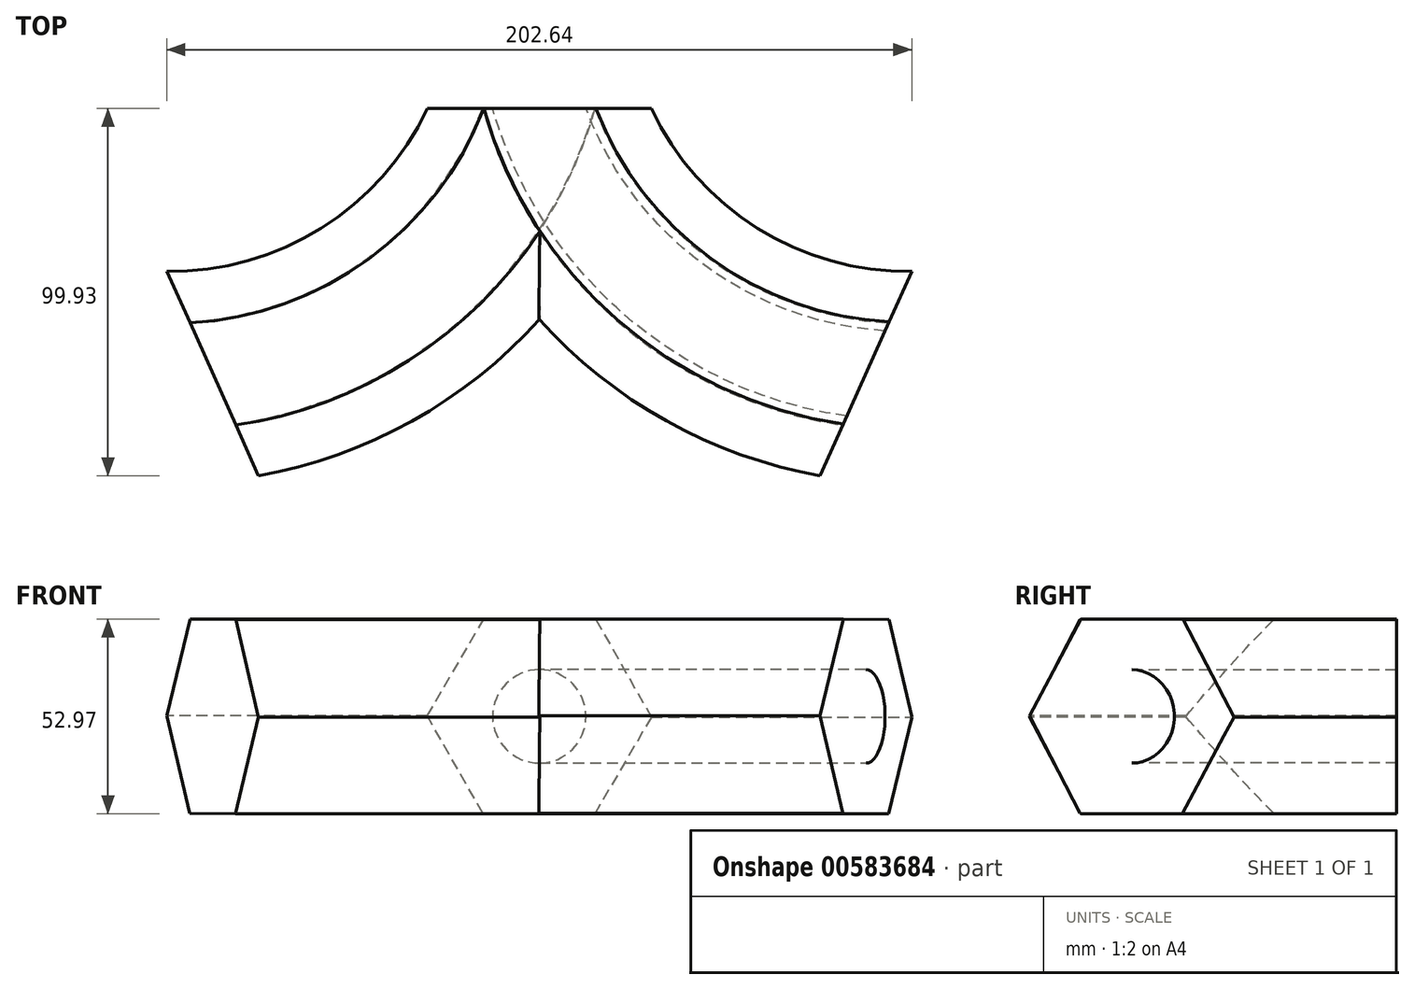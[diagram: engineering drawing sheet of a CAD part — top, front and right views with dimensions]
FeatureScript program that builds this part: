
annotation { "Feature Type Name" : "Feature", "Feature Type Description" : "" }
export const myFeature = defineFeature(function(context is Context, id is Id, definition is map)
    precondition{}
    {
        {
            var Q0;
            Q0=qCreatedBy(makeId("Front.planeOp"),FACE);
            var sketch = newSketch(context, id + "F0", { "sketchPlane" : qUnion([Q0])});
            skCircle(sketch, "E0.cCircle", {"center": v(0, 26.89) * mm, "radius": 26.4 * mm, "construction": true});
            skLineSegment(sketch, "E0.0", {"start": v(-15.4, 0.58) * mm, "end": v(-30.48, 27.07) * mm});
            skLineSegment(sketch, "E0.1", {"start": v(-30.48, 27.07) * mm, "end": v(-15.08, 53.37) * mm});
            skLineSegment(sketch, "E0.2", {"start": v(-15.08, 53.37) * mm, "end": v(15.4, 53.2) * mm});
            skLineSegment(sketch, "E0.3", {"start": v(15.4, 53.2) * mm, "end": v(30.48, 26.7) * mm});
            skLineSegment(sketch, "E0.4", {"start": v(30.48, 26.7) * mm, "end": v(15.08, 0.4) * mm});
            skLineSegment(sketch, "E0.5", {"start": v(15.08, 0.4) * mm, "end": v(-15.4, 0.58) * mm});
            skPoint(sketch, "E0.0.midPoint", {"position": v(-22.94, 13.82) * mm});
            skCircle(sketch, "E1", {"center": v(0, 26.89) * mm, "radius": 12.7 * mm});
            skSolve(sketch);
        }
        {
            var Q0;
            Q0=qCreatedBy(makeId("Top.planeOp"),FACE);
            var sketch = newSketch(context, id + "F1", { "sketchPlane" : qUnion([Q0])});
            skArc(sketch, "E2", {"start": v(-88.86, -72.11) * mm, "mid": v(-33.77, -49.2) * mm, "end": v(0, 0) * mm});
            skArc(sketch, "E3.MirrorCS", {"start": v(88.86, -72.11) * mm, "mid": v(33.77, -49.2) * mm, "end": v(0, 0) * mm});
            skSolve(sketch);
        }
        {
            var Q0;
            Q0=makeQuery(id+"F0.imprint","IMPRINT",FACE,{"disambiguationData":[TD([[makeQuery(id+"F0.imprint","IMPRINT",EDGE,{"derivedFrom":sQuery(id+"F0.wireOp",EDGE,"E0.0")}),-1.0]])]});
            var Q1;
            Q1=makeQuery(id+"F0.imprint","IMPRINT",FACE,{"disambiguationData":[TD([[makeQuery(id+"F0.imprint","IMPRINT",EDGE,{"derivedFrom":sQuery(id+"F0.wireOp",EDGE,"E1")}),1.0]])]});
            var Q2;
            Q2=sQuery(id+"F1.wireOp",EDGE,"E3.MirrorCS");
            sweep(context, id + "F2", {"profiles" : qUnion([Q0, Q1]), "path" : qUnion([Q2])});
        }
        {
            var Q0;
            Q0=makeQuery(id+"F0.imprint","IMPRINT",FACE,{"disambiguationData":[TD([[makeQuery(id+"F0.imprint","IMPRINT",EDGE,{"derivedFrom":sQuery(id+"F0.wireOp",EDGE,"E0.0")}),-1.0]])]});
            var Q1;
            Q1=makeQuery(id+"F0.imprint","IMPRINT",FACE,{"disambiguationData":[TD([[makeQuery(id+"F0.imprint","IMPRINT",EDGE,{"derivedFrom":sQuery(id+"F0.wireOp",EDGE,"E1")}),1.0]])]});
            var Q2;
            Q2=sQuery(id+"F1.wireOp",EDGE,"E2");
            sweep(context, id + "F3", {"operationType" : NewBodyOperationType.ADD, "profiles" : qUnion([Q0, Q1]), "path" : qUnion([Q2])});
        }
        {
            var Q0;
            Q0=makeQuery(id+"F0.imprint","IMPRINT",FACE,{"disambiguationData":[TD([[makeQuery(id+"F0.imprint","IMPRINT",EDGE,{"derivedFrom":sQuery(id+"F0.wireOp",EDGE,"E1")}),1.0]])]});
            var Q1;
            Q1=sQuery(id+"F1.wireOp",EDGE,"E3.MirrorCS");
            sweep(context, id + "F4", {"operationType" : NewBodyOperationType.REMOVE, "profiles" : qUnion([Q0]), "path" : qUnion([Q1])});
        }
    });
